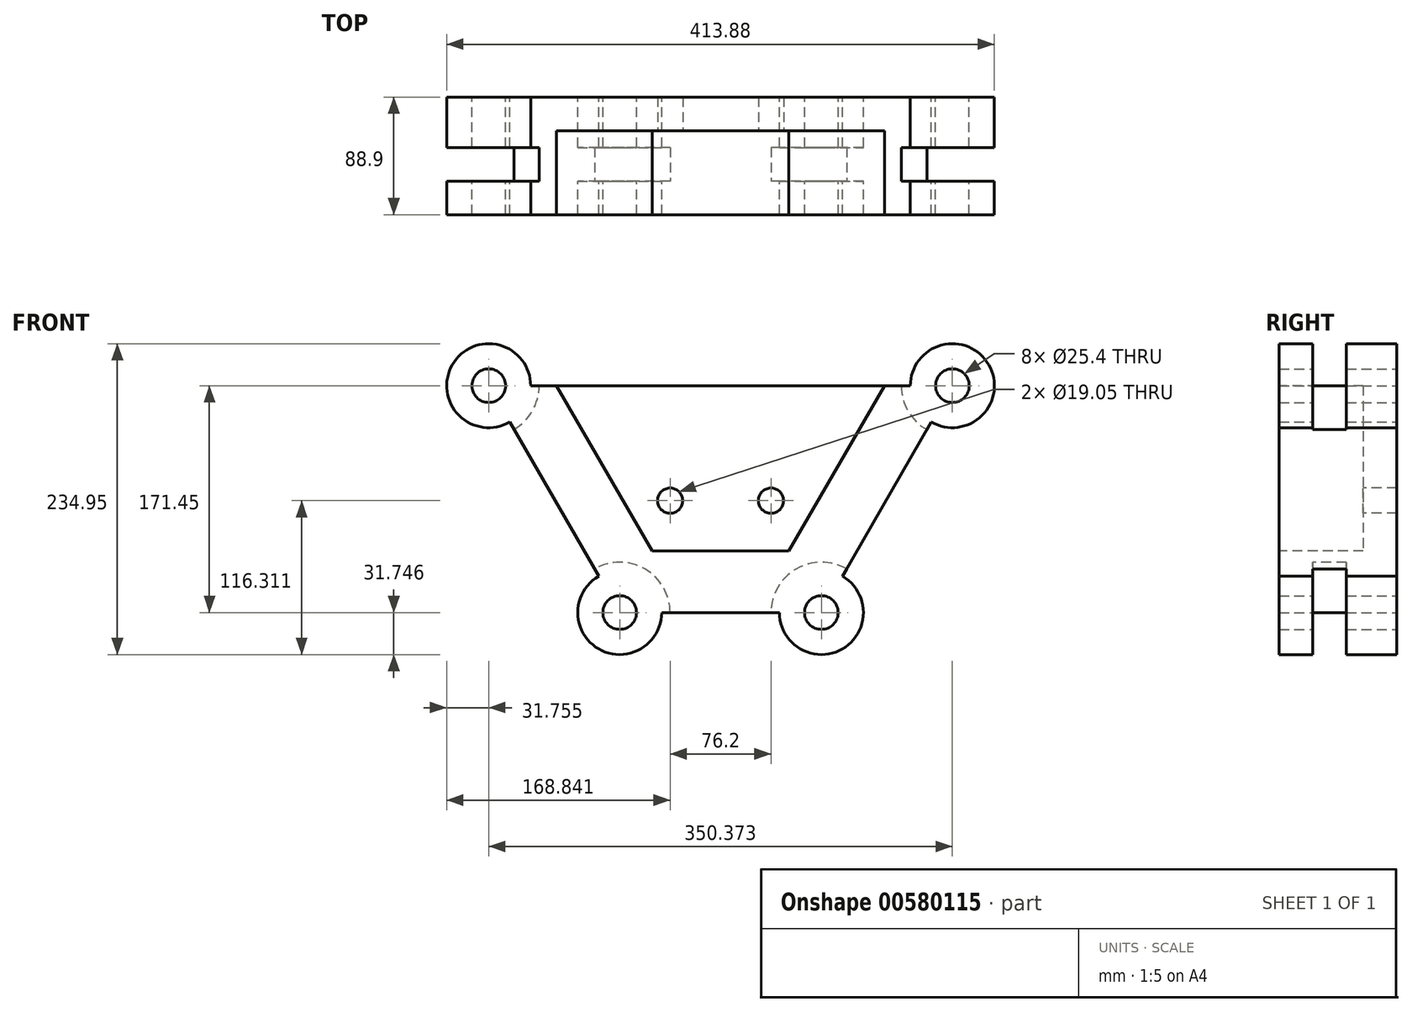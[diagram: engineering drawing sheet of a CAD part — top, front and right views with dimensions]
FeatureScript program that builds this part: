
annotation { "Feature Type Name" : "Feature", "Feature Type Description" : "" }
export const myFeature = defineFeature(function(context is Context, id is Id, definition is map)
    precondition{}
    {
        {
            var Q0;
            Q0=qCreatedBy(makeId("Front.planeOp"),FACE);
            var sketch = newSketch(context, id + "F0", { "sketchPlane" : qUnion([Q0])});
            skLineSegment(sketch, "E0", {"start": v(-74.79, 41.05) * mm, "end": v(262.89, 41.05) * mm});
            skLineSegment(sketch, "E1", {"start": v(262.89, 41.05) * mm, "end": v(163.9, -130.4) * mm});
            skLineSegment(sketch, "E2", {"start": v(163.9, -130.4) * mm, "end": v(11.5, -130.4) * mm});
            skLineSegment(sketch, "E3", {"start": v(11.5, -130.4) * mm, "end": v(-81.14, 30.05) * mm});
            skCircle(sketch, "E4", {"center": v(-87.49, 41.05) * mm, "radius": 12.7 * mm});
            skCircle(sketch, "E5", {"center": v(262.89, 41.05) * mm, "radius": 12.7 * mm});
            skCircle(sketch, "E6", {"center": v(11.5, -130.4) * mm, "radius": 12.7 * mm});
            skCircle(sketch, "E7", {"center": v(11.5, -130.4) * mm, "radius": 31.75 * mm});
            skCircle(sketch, "E8", {"center": v(163.9, -130.4) * mm, "radius": 12.7 * mm});
            skCircle(sketch, "E9", {"center": v(163.9, -130.4) * mm, "radius": 31.75 * mm});
            skCircle(sketch, "E10", {"center": v(-87.49, 41.05) * mm, "radius": 31.75 * mm});
            skCircle(sketch, "E11", {"center": v(262.89, 41.05) * mm, "radius": 31.75 * mm});
            skSolve(sketch);
        }
        {
            var Q0;
            {var subQ0=sQuery(id+"F0.wireOp",EDGE,"E4");var subQ1=sQuery(id+"F0.wireOp",EDGE,"E0");var subQ2=makeQuery(id+"F0.imprint","INTERSECT",VERTEX,{"derivedFrom":[subQ1,subQ0]});Q0=makeQuery(id+"F0.imprint","IMPRINT",FACE,{"disambiguationData":[TD([[makeQuery(id+"F0.imprint","IMPRINT",EDGE,{"disambiguationData":[TD([[subQ2,-1.0]])],"derivedFrom":subQ1}),1.0]])]});}
            var Q1;
            {var subQ0=sQuery(id+"F0.wireOp",EDGE,"E11");var subQ1=sQuery(id+"F0.wireOp",EDGE,"E0");var subQ2=makeQuery(id+"F0.imprint","INTERSECT",VERTEX,{"derivedFrom":[subQ1,subQ0]});Q1=makeQuery(id+"F0.imprint","IMPRINT",FACE,{"disambiguationData":[TD([[makeQuery(id+"F0.imprint","IMPRINT",EDGE,{"disambiguationData":[TD([[subQ2,-1.0]])],"derivedFrom":subQ1}),1.0]])]});}
            var Q2;
            {var subQ0=sQuery(id+"F0.wireOp",EDGE,"E9");var subQ1=sQuery(id+"F0.wireOp",EDGE,"E1");var subQ2=makeQuery(id+"F0.imprint","INTERSECT",VERTEX,{"derivedFrom":[subQ1,subQ0]});Q2=makeQuery(id+"F0.imprint","IMPRINT",FACE,{"disambiguationData":[TD([[makeQuery(id+"F0.imprint","IMPRINT",EDGE,{"disambiguationData":[TD([[subQ2,-1.0]])],"derivedFrom":subQ1}),1.0]])]});}
            var Q3;
            {var subQ0=sQuery(id+"F0.wireOp",EDGE,"E7");var subQ1=sQuery(id+"F0.wireOp",EDGE,"E2");var subQ2=makeQuery(id+"F0.imprint","INTERSECT",VERTEX,{"derivedFrom":[subQ1,subQ0]});Q3=makeQuery(id+"F0.imprint","IMPRINT",FACE,{"disambiguationData":[TD([[makeQuery(id+"F0.imprint","IMPRINT",EDGE,{"disambiguationData":[TD([[subQ2,-1.0]])],"derivedFrom":subQ1}),1.0]])]});}
            var Q4;
            {var subQ0=sQuery(id+"F0.wireOp",EDGE,"E7");var subQ1=sQuery(id+"F0.wireOp",EDGE,"E2");var subQ2=makeQuery(id+"F0.imprint","INTERSECT",VERTEX,{"derivedFrom":[subQ1,subQ0]});Q4=makeQuery(id+"F0.imprint","IMPRINT",FACE,{"disambiguationData":[TD([[makeQuery(id+"F0.imprint","IMPRINT",EDGE,{"disambiguationData":[TD([[subQ2,-1.0]])],"derivedFrom":subQ1}),-1.0]])]});}
            var Q5;
            {var subQ0=sQuery(id+"F0.wireOp",EDGE,"E4");var subQ1=sQuery(id+"F0.wireOp",EDGE,"E0");var subQ2=makeQuery(id+"F0.imprint","INTERSECT",VERTEX,{"derivedFrom":[subQ1,subQ0]});Q5=makeQuery(id+"F0.imprint","IMPRINT",FACE,{"disambiguationData":[TD([[makeQuery(id+"F0.imprint","IMPRINT",EDGE,{"disambiguationData":[TD([[subQ2,-1.0]])],"derivedFrom":subQ1}),-1.0]])]});}
            var Q6;
            {var subQ0=sQuery(id+"F0.wireOp",EDGE,"E11");var subQ1=sQuery(id+"F0.wireOp",EDGE,"E0");var subQ2=makeQuery(id+"F0.imprint","INTERSECT",VERTEX,{"derivedFrom":[subQ1,subQ0]});Q6=makeQuery(id+"F0.imprint","IMPRINT",FACE,{"disambiguationData":[TD([[makeQuery(id+"F0.imprint","IMPRINT",EDGE,{"disambiguationData":[TD([[subQ2,-1.0]])],"derivedFrom":subQ1}),-1.0]])]});}
            var Q7;
            {var subQ0=sQuery(id+"F0.wireOp",EDGE,"E9");var subQ1=sQuery(id+"F0.wireOp",EDGE,"E1");var subQ2=makeQuery(id+"F0.imprint","INTERSECT",VERTEX,{"derivedFrom":[subQ1,subQ0]});Q7=makeQuery(id+"F0.imprint","IMPRINT",FACE,{"disambiguationData":[TD([[makeQuery(id+"F0.imprint","IMPRINT",EDGE,{"disambiguationData":[TD([[subQ2,-1.0]])],"derivedFrom":subQ1}),-1.0]])]});}
            var Q8;
            {var subQ3=sQuery(id+"F0.wireOp",EDGE,"E10");var subQ13=sQuery(id+"F0.wireOp",EDGE,"E0");var subQ14=makeQuery(id+"F0.imprint","INTERSECT",VERTEX,{"derivedFrom":[subQ13,subQ3]});Q8=makeQuery(id+"F0.imprint","IMPRINT",FACE,{"disambiguationData":[TD([[makeQuery(id+"F0.imprint","IMPRINT",EDGE,{"disambiguationData":[TD([[subQ14,-1.0]])],"derivedFrom":subQ13}),-1.0]])]});}
            extrude(context, id + "F1", {"entities" : qUnion([Q0, Q1, Q2, Q3, Q4, Q5, Q6, Q7, Q8]), "endBound" : BoundingType.SYMMETRIC, "depth" : 101.6 * mm, "offsetDistance" : 25.4 * mm});
        }
        {
            var Q0;
            Q0=makeQuery(id+"F1.opExtrude","CAP_FACE",FACE,{"disambiguationData":[OSD([sQuery(id+"F0.wireOp",EDGE,"E0"),sQuery(id+"F0.wireOp",EDGE,"E1"),sQuery(id+"F0.wireOp",EDGE,"E2"),sQuery(id+"F0.wireOp",EDGE,"E3"),sQuery(id+"F0.wireOp",EDGE,"E4"),sQuery(id+"F0.wireOp",EDGE,"E5"),sQuery(id+"F0.wireOp",EDGE,"E6"),sQuery(id+"F0.wireOp",EDGE,"E7"),sQuery(id+"F0.wireOp",EDGE,"E8"),sQuery(id+"F0.wireOp",EDGE,"E9"),sQuery(id+"F0.wireOp",EDGE,"E10"),sQuery(id+"F0.wireOp",EDGE,"E11")])],"isStart":false});
            var sketch = newSketch(context, id + "F2", { "sketchPlane" : qUnion([Q0])});
            skLineSegment(sketch, "E12", {"start": v(-36.16, 41.05) * mm, "end": v(36, -83.94) * mm});
            skLineSegment(sketch, "E13", {"start": v(36, -83.94) * mm, "end": v(139.4, -83.94) * mm});
            skLineSegment(sketch, "E14", {"start": v(139.4, -83.94) * mm, "end": v(211.56, 41.05) * mm});
            skSolve(sketch);
        }
        {
            var Q0;
            {var subQ0=sQuery(id+"F2.wireOp",EDGE,"E12");Q0=makeQuery(id+"F2.imprint","IMPRINT",FACE,{"disambiguationData":[TD([[makeQuery(id+"F2.imprint","IMPRINT",EDGE,{"derivedFrom":subQ0}),1.0]])]});}
            extrude(context, id + "F3", {"entities" : qUnion([Q0]), "operationType" : NewBodyOperationType.REMOVE, "oppositeDirection" : true, "depth" : 76.2 * mm, "offsetDistance" : 25.4 * mm});
        }
        {
            var Q0;
            Q0=qCreatedBy(makeId("Front.planeOp"),FACE);
            var sketch = newSketch(context, id + "F4", { "sketchPlane" : qUnion([Q0])});
            skCircle(sketch, "E15", {"center": v(-87.5, 41.04) * mm, "radius": 38.1 * mm});
            skCircle(sketch, "E16", {"center": v(262.28, 41.05) * mm, "radius": 38.1 * mm});
            skCircle(sketch, "E17", {"center": v(163.9, -130.4) * mm, "radius": 38.1 * mm});
            skCircle(sketch, "E18", {"center": v(11.5, -130.4) * mm, "radius": 38.1 * mm});
            skSolve(sketch);
        }
        {
            var Q0;
            Q0=makeQuery(id+"F4.imprint","IMPRINT",FACE,{"disambiguationData":[TD([[makeQuery(id+"F4.imprint","IMPRINT",EDGE,{"derivedFrom":sQuery(id+"F4.wireOp",EDGE,"E15")}),1.0]])]});
            var Q1;
            Q1=makeQuery(id+"F4.imprint","IMPRINT",FACE,{"disambiguationData":[TD([[makeQuery(id+"F4.imprint","IMPRINT",EDGE,{"derivedFrom":sQuery(id+"F4.wireOp",EDGE,"E16")}),1.0]])]});
            var Q2;
            Q2=makeQuery(id+"F4.imprint","IMPRINT",FACE,{"disambiguationData":[TD([[makeQuery(id+"F4.imprint","IMPRINT",EDGE,{"derivedFrom":sQuery(id+"F4.wireOp",EDGE,"E17")}),1.0]])]});
            var Q3;
            Q3=makeQuery(id+"F4.imprint","IMPRINT",FACE,{"disambiguationData":[TD([[makeQuery(id+"F4.imprint","IMPRINT",EDGE,{"derivedFrom":sQuery(id+"F4.wireOp",EDGE,"E18")}),1.0]])]});
            var Q4;
            Q4=makeQuery(id+"F1.opExtrude","CAP_FACE",FACE,{"disambiguationData":[OSD([sQuery(id+"F0.wireOp",EDGE,"E0"),sQuery(id+"F0.wireOp",EDGE,"E1"),sQuery(id+"F0.wireOp",EDGE,"E2"),sQuery(id+"F0.wireOp",EDGE,"E3"),sQuery(id+"F0.wireOp",EDGE,"E4"),sQuery(id+"F0.wireOp",EDGE,"E5"),sQuery(id+"F0.wireOp",EDGE,"E6"),sQuery(id+"F0.wireOp",EDGE,"E7"),sQuery(id+"F0.wireOp",EDGE,"E8"),sQuery(id+"F0.wireOp",EDGE,"E9"),sQuery(id+"F0.wireOp",EDGE,"E10"),sQuery(id+"F0.wireOp",EDGE,"E11")])],"isStart":false});
            extrude(context, id + "F5", {"entities" : qUnion([Q0, Q1, Q2, Q3, Q4]), "operationType" : NewBodyOperationType.REMOVE, "endBound" : BoundingType.SYMMETRIC, "oppositeDirection" : true, "depth" : 25.4 * mm, "offsetDistance" : 25.4 * mm});
        }
        {
            var Q0;
            Q0=makeQuery(id+"F3.boolean.opBoolean","COPY",FACE,{"derivedFrom":makeQuery(id+"F3.opExtrude","CAP_FACE",FACE,{"disambiguationData":[OSD([sQuery(id+"F0.wireOp",EDGE,"E0"),sQuery(id+"F2.wireOp",EDGE,"E12"),sQuery(id+"F2.wireOp",EDGE,"E13"),sQuery(id+"F2.wireOp",EDGE,"E14")])],"isStart":false})});
            var sketch = newSketch(context, id + "F6", { "sketchPlane" : qUnion([Q0])});
            skLineSegment(sketch, "E19", {"start": v(87.7, -83.94) * mm, "end": v(87.7, -45.84) * mm, "construction": true});
            skLineSegment(sketch, "E20", {"start": v(125.8, -45.84) * mm, "end": v(49.6, -45.84) * mm, "construction": true});
            skCircle(sketch, "E21", {"center": v(49.6, -45.84) * mm, "radius": 9.53 * mm});
            skCircle(sketch, "E22", {"center": v(125.8, -45.84) * mm, "radius": 9.53 * mm});
            skSolve(sketch);
        }
        {
            var Q0;
            Q0=makeQuery(id+"F6.imprint","IMPRINT",FACE,{"disambiguationData":[TD([[makeQuery(id+"F6.imprint","IMPRINT",EDGE,{"derivedFrom":sQuery(id+"F6.wireOp",EDGE,"E21")}),1.0]])]});
            var Q1;
            Q1=makeQuery(id+"F6.imprint","IMPRINT",FACE,{"disambiguationData":[TD([[makeQuery(id+"F6.imprint","IMPRINT",EDGE,{"derivedFrom":sQuery(id+"F6.wireOp",EDGE,"E22")}),1.0]])]});
            extrude(context, id + "F7", {"entities" : qUnion([Q0, Q1]), "operationType" : NewBodyOperationType.REMOVE, "endBound" : BoundingType.THROUGH_ALL, "oppositeDirection" : true, "depth" : 25.4 * mm, "offsetDistance" : 25.4 * mm});
        }
    });
